# Revit family: B-39003
name_source: partatom
category: Specialty Equipment
units: mm (PartAtom-declared; Revit-internal decimal feet)

## family parameters
Cut with Voids When Loaded = No
Host = Face
OmniClass Number = 23.40.20.21
OmniClass Title = Toilet and Bath Specialties
Part Type = Normal
Room Calculation Point = No
Round Connector Dimension = Use Diameter
Shared = No

## types (1)
- B-39003
    Assembly Code = E1090900
    Capacity = 600 C-fold Towels  ;  800 Multifold Towels  ;  1100 Singlefold Towels  ;  12 gal Waste
    Default Elevation = 48"
    Description = Bobrick B-39003 TrimLine Series Recessed Combination Towel and Waste Unit
    Finish = Stainless Steel-Bobrick-Type 304-Satin
    Installation-Fabrication = http://www.bobrick.com
    Keynote = 102813
    Manufacturer = Bobrick Washroom Equipment, Inc.
    Manufacturer Fax = 818-503-1930
    Manufacturer Website = http://www.bobrick.com
    Materials = Stainless Steel-Bobrick-Type 304-Satin
    Model = B-39003
    Product Documentation Link = https://www.bobrick.com
    Product Page URL = https://www.bobrick.com
    Recess Into Host = 7 5/8"
    Revised Date = 11/03/2020
    Send Message = http://www.arcat.com
    URL = http://www.bobrick.com
    Unit Depth = 8 3/16"
    Unit Height = 56"
    Unit Width = 17 3/16"

## geometry (parser evidence)
native form markers: Blend x2, Sweep x3
no freeform markers — native parametric forms only
